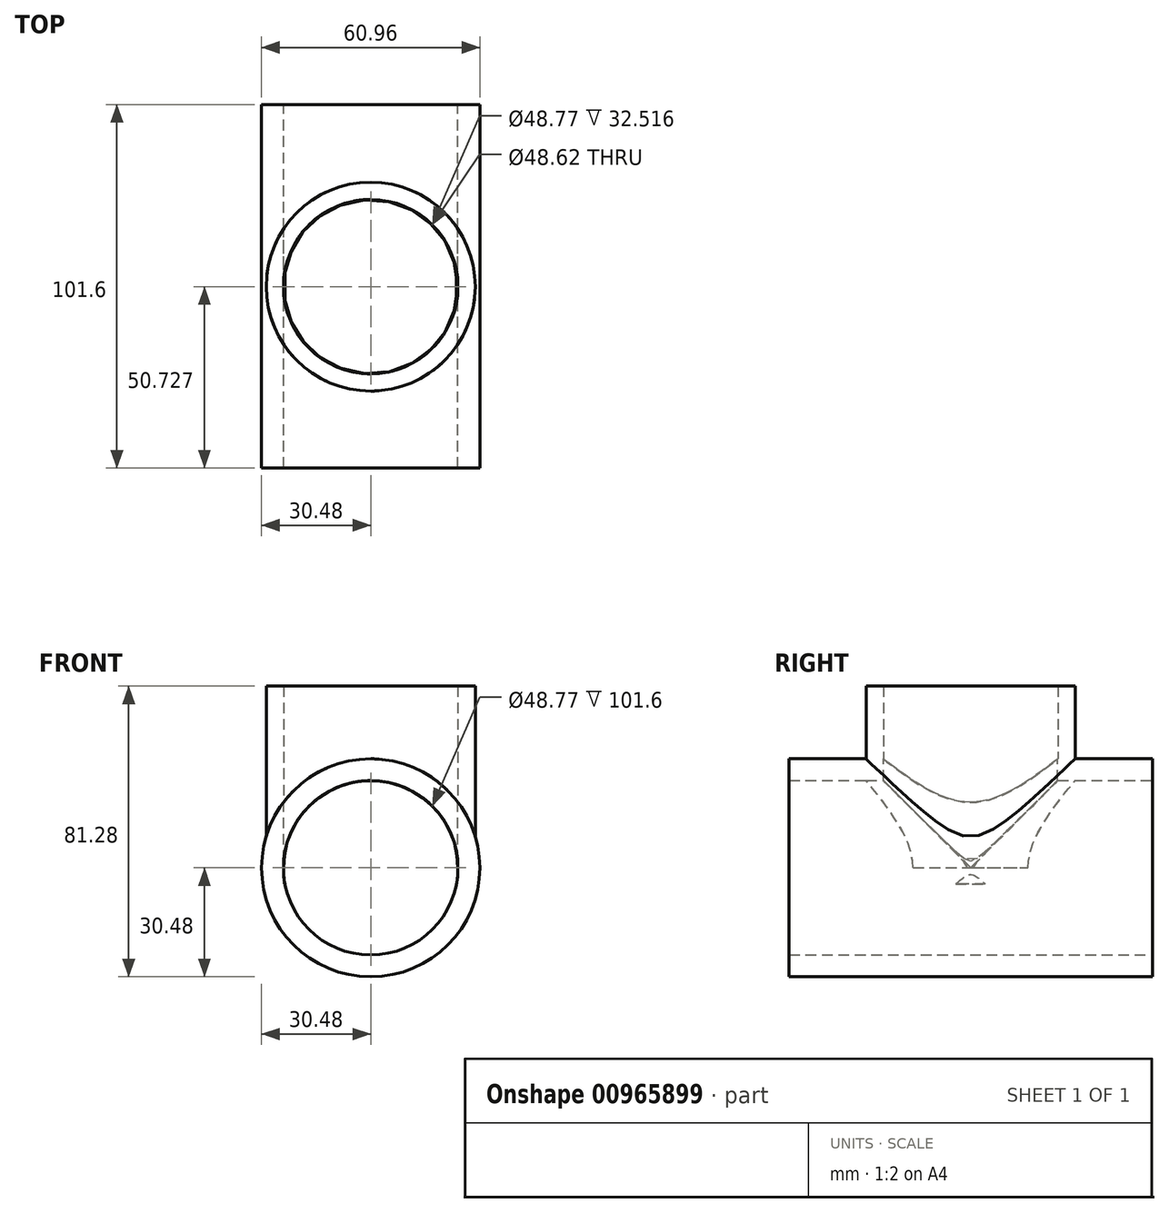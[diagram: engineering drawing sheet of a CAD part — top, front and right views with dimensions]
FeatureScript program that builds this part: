
annotation { "Feature Type Name" : "Feature", "Feature Type Description" : "" }
export const myFeature = defineFeature(function(context is Context, id is Id, definition is map)
    precondition{}
    {
        {
            var Q0;
            Q0=qCreatedBy(makeId("Front.planeOp"),FACE);
            var sketch = newSketch(context, id + "F0", { "sketchPlane" : qUnion([Q0])});
            skCircle(sketch, "E0", {"center": v(0, 0) * mm, "radius": 24.38 * mm});
            skCircle(sketch, "E1", {"center": v(0, 0) * mm, "radius": 30.48 * mm});
            skSolve(sketch);
        }
        {
            var Q0;
            Q0=qSketchRegion(id+"F0",true);
            extrude(context, id + "F1", {"entities" : qUnion([Q0]), "depth" : 101.6 * mm, "offsetDistance" : 25.4 * mm});
        }
        {
            var Q0;
            Q0=qCreatedBy(makeId("Top.planeOp"),FACE);
            var sketch = newSketch(context, id + "F2", { "sketchPlane" : qUnion([Q0])});
            skLineSegment(sketch, "E2", {"start": v(0, 0) * mm, "end": v(0, -101.75) * mm});
            skCircle(sketch, "E3", {"center": v(0, -50.87) * mm, "radius": 24.38 * mm});
            skCircle(sketch, "E4", {"center": v(0, -50.87) * mm, "radius": 29.21 * mm});
            skSolve(sketch);
        }
        {
            var Q0;
            Q0=qSketchRegion(id+"F2",true);
            extrude(context, id + "F3", {"entities" : qUnion([Q0]), "operationType" : NewBodyOperationType.ADD, "depth" : 50.8 * mm, "offsetDistance" : 25.4 * mm});
        }
        {
            var Q0;
            Q0=makeQuery(id+"F3.opExtrude","CAP_FACE",FACE,{"disambiguationData":[OSD([sQuery(id+"F2.wireOp",EDGE,"E3"),sQuery(id+"F2.wireOp",EDGE,"E4")])],"isStart":false});
            var sketch = newSketch(context, id + "F4", { "sketchPlane" : qUnion([Q0])});
            skCircle(sketch, "E5", {"center": v(0, -50.87) * mm, "radius": 24.31 * mm});
            skSolve(sketch);
        }
        {
            var Q0;
            Q0=makeQuery(id+"F4.imprint","IMPRINT",FACE,{"disambiguationData":[TD([[makeQuery(id+"F4.imprint","IMPRINT",EDGE,{"derivedFrom":sQuery(id+"F4.wireOp",EDGE,"E5")}),1.0]])]});
            extrude(context, id + "F5", {"entities" : qUnion([Q0]), "operationType" : NewBodyOperationType.REMOVE, "oppositeDirection" : true, "depth" : 55.37 * mm, "offsetDistance" : 25.4 * mm});
        }
        {
            var Q0;
            Q0=makeQuery(id+"F1.opExtrude","CAP_FACE",FACE,{"disambiguationData":[OSD([sQuery(id+"F0.wireOp",EDGE,"E0"),sQuery(id+"F0.wireOp",EDGE,"E1")])],"isStart":true});
            var sketch = newSketch(context, id + "F6", { "sketchPlane" : qUnion([Q0])});
            skCircle(sketch, "E6", {"center": v(0, 0) * mm, "radius": 24.37 * mm});
            skSolve(sketch);
        }
        {
            var Q0;
            Q0=makeQuery(id+"F6.imprint","IMPRINT",FACE,{"disambiguationData":[TD([[makeQuery(id+"F6.imprint","IMPRINT",EDGE,{"derivedFrom":sQuery(id+"F6.wireOp",EDGE,"E6")}),1.0]])]});
            extrude(context, id + "F7", {"entities" : qUnion([Q0]), "operationType" : NewBodyOperationType.REMOVE, "oppositeDirection" : true, "depth" : 105.66 * mm, "offsetDistance" : 25.4 * mm});
        }
    });
